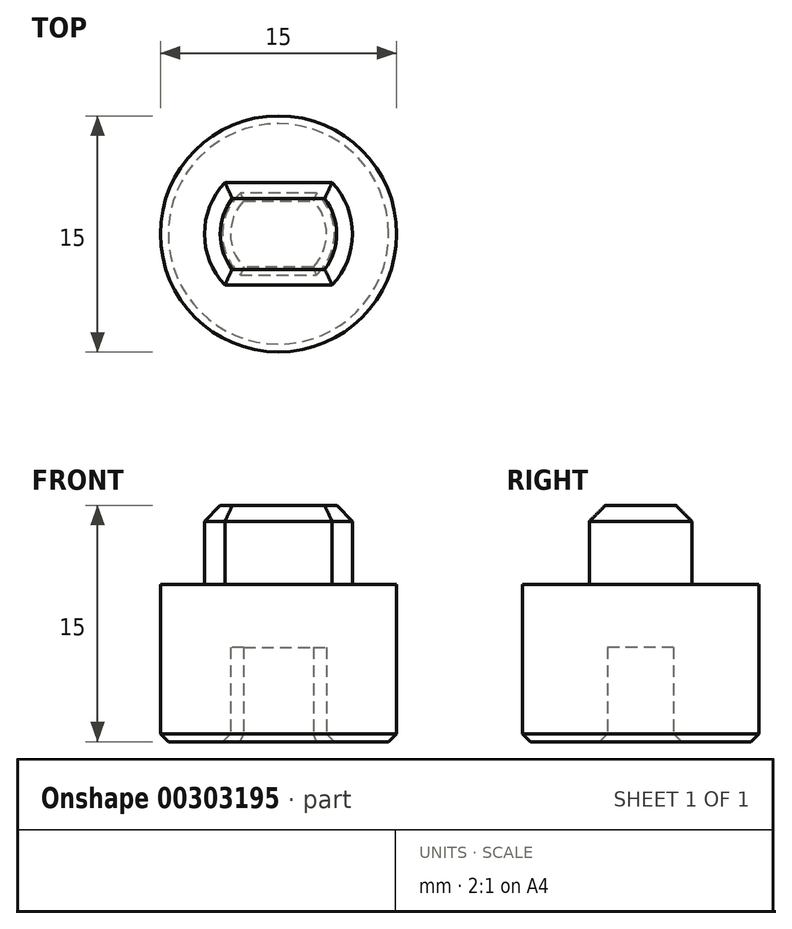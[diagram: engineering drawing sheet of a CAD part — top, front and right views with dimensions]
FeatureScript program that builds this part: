
annotation { "Feature Type Name" : "Feature", "Feature Type Description" : "" }
export const myFeature = defineFeature(function(context is Context, id is Id, definition is map)
    precondition{}
    {
        {
            var Q0;
            Q0=qCreatedBy(makeId("Top.planeOp"),FACE);
            var sketch = newSketch(context, id + "F0", { "sketchPlane" : qUnion([Q0])});
            skLineSegment(sketch, "E0", {"start": v(-3.4, 3.25) * mm, "end": v(3.4, 3.25) * mm});
            skLineSegment(sketch, "E1", {"start": v(-3.4, -3.25) * mm, "end": v(3.4, -3.25) * mm});
            skArc(sketch, "E2", {"start": v(3.4, -3.25) * mm, "mid": v(4.7, 0) * mm, "end": v(3.4, 3.25) * mm});
            skArc(sketch, "E3.trimOffspring", {"start": v(-3.4, 3.25) * mm, "mid": v(-4.7, 0) * mm, "end": v(-3.4, -3.25) * mm});
            skSolve(sketch);
        }
        {
            var Q0;
            Q0=qCreatedBy(makeId("Top.planeOp"),FACE);
            var sketch = newSketch(context, id + "F1", { "sketchPlane" : qUnion([Q0])});
            skCircle(sketch, "E4", {"center": v(0, 0) * mm, "radius": 7.5 * mm});
            skSolve(sketch);
        }
        {
            var Q0;
            Q0 = qSketchRegion(id + "F1", true);
            extrude(context, id + "F2", {"entities" : qUnion([Q0]), "depth" : 10 * mm});
        }
        {
            var Q0;
            Q0 = qSketchRegion(id + "F0", true);
            extrude(context, id + "F3", {"entities" : qUnion([Q0]), "operationType" : NewBodyOperationType.ADD, "depth" : 15 * mm, "hasSecondDirection" : true, "secondDirectionOppositeDirection" : false, "secondDirectionDepth" : 10 * mm});
        }
        {
            var Q0;
            Q0=makeQuery(id+"F3.opExtrude","CAP_FACE",FACE,{"disambiguationData":[OSD([sQuery(id+"F0.wireOp",EDGE,"E0"),sQuery(id+"F0.wireOp",EDGE,"E1"),sQuery(id+"F0.wireOp",EDGE,"E2"),sQuery(id+"F0.wireOp",EDGE,"E3.trimOffspring")])],"isStart":false});
            chamfer(context, id + "F4", {"entities" : qUnion([Q0]), "width" : 1 * mm, "tangentPropagation" : true});
        }
        {
            var Q0;
            Q0=makeQuery(id+"F2.opExtrude","CAP_FACE",FACE,{"disambiguationData":[OSD([sQuery(id+"F1.wireOp",EDGE,"E4")])],"isStart":true});
            var sketch = newSketch(context, id + "F5", { "sketchPlane" : qUnion([Q0])});
            skArc(sketch, "E5", {"start": v(2.21, -2.1) * mm, "mid": v(3.05, 0) * mm, "end": v(2.21, 2.1) * mm});
            skLineSegment(sketch, "E6", {"start": v(-2.21, 2.1) * mm, "end": v(2.21, 2.1) * mm});
            skLineSegment(sketch, "E7.MirrorCS", {"start": v(-2.21, -2.1) * mm, "end": v(2.21, -2.1) * mm});
            skPoint(sketch, "E8.orphan", {"position": v(4.78, -2.1) * mm});
            skPoint(sketch, "E9.orphan", {"position": v(-4.87, -2.1) * mm});
            skPoint(sketch, "E10.orphan", {"position": v(-4.87, 2.1) * mm});
            skPoint(sketch, "E11.orphan", {"position": v(4.78, 2.1) * mm});
            skArc(sketch, "E12.trimOffspring", {"start": v(-2.21, 2.1) * mm, "mid": v(-3.05, 0) * mm, "end": v(-2.21, -2.1) * mm});
            skSolve(sketch);
        }
        {
            var Q0;
            Q0 = qSketchRegion(id + "F5", true);
            extrude(context, id + "F6", {"entities" : qUnion([Q0]), "operationType" : NewBodyOperationType.REMOVE, "oppositeDirection" : true, "depth" : 6 * mm});
        }
        {
            var Q0;
            Q0=makeQuery(id+"F2.opExtrude","CAP_FACE",FACE,{"disambiguationData":[OSD([sQuery(id+"F1.wireOp",EDGE,"E4")])],"isStart":true});
            chamfer(context, id + "F7", {"entities" : qUnion([Q0]), "width" : 0.5 * mm, "tangentPropagation" : true});
        }
    });
